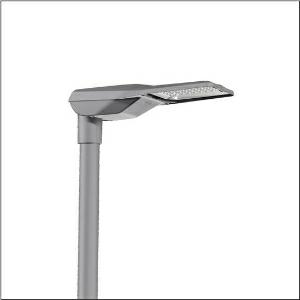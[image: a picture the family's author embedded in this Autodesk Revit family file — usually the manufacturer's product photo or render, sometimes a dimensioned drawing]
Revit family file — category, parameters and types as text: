
# Revit family: streetlight_sl_21_iq_mini___pl52_5xe2h31g08gb_d0f1
name_source: partatom
category: Lighting Fixtures
units: mm (PartAtom-declared; Revit-internal decimal feet)

## family parameters
Cut with Voids When Loaded = No
Host = Face
Light Source = No
Part Type = Normal
Room Calculation Point = No
Round Connector Dimension = Use Diameter
Shared = No

## types (1)
- --- (1 x LED, 5580 lm, 37.1 W, 3000K)
    Apparent Load = 37 VA
    CIE Flux Codes = 27 59 98 100 100
    Color Rendering = 70
    Color Temperature = 3000K
    Default Elevation = 1800 mm
    Description = Streetlight SL 21 iQ mini, mast luminaire, primary light control with lens, of PMMA, primary optical cover: cover, of toughened safety glass, transparent, light distribution: PL52, light emission: direct distribution, primary light characteristic: asymmetric, installation type: post-top, side-entry, LED, High Power LED, rated luminous flux: 5.580lm, luminous efficacy: 150lm/W, light colour: 730, colour temperature: 3000K, control gear: iQ Street-Remote, control: Street-Remote, Auto-Match, Temp-Guard, Lumen-Switch, Night-Set, Smart-Wire, Light-Fading, Desk-Remote (wireless, voltage-free reading and setting of iQ features in the workshop via application-optimized NFC function/RFID function), optimised constant luminous flux control (CLO 2.0), pre-setting: linear dimming characteristic, mains connection: 220..240V, AC, 50/60Hz, start of lifetime: 37W, end of service life: 39W, reduction: 18W, luminaire housing, of diecast aluminium, powder-coated, SITECO metallic grey (DB 702S), corrosivity category C5 high according to DIN EN ISO 12944, please order mast flange separately, inclination adjustable: 0°, 5°, 10°, 15°, sealing non-destructively replaceable, multi-level sealing system, length: 628mm, width: 235mm, height: 110mm, mast flange for spigot size: 42mm (side-entry): 5XC10008XM4, 60/48mm (side-entry/post-top): 5XC10108XM2, 76/60mm (side-entry/post-top): 5XC10108XM1, mounting height: 4..8m, protection rating (complete): IP66, insulation class (complete): insulation class II (safety insulation), certification: CE, ENEC, ENEC+, VDE, impact resistance: IK10, permissible operating ambient temperature for outdoor applications: -40..+50°C, standard-compliant lighting for roads and squares, packaging unit: 1 piece

Light Distribution: PL52
    Height = 110 mm
    Lamp = 1 x LED
    Lamp Light Flux = 5580 lm
    Lamp Power = 37.1 W
    Lamp count = 1
    Length = 625 mm
    Luminous efficacy = 150 lm/W
    Manufacturer = Siteco
    ModVariant = No
    Model = 5XE2H31G08GB
    Number of Poles = 1
    OnlyDefault = Yes
    Power Factor = 1
    Product Name = Streetlight SL 21 iQ mini | PL52
    Product group = mast luminaire | pylon top
    ProductGroupID = 6100
    Protection Class = Protection class II
    Protection Degree = IP 66
    RLX_Detail_Level = 1
    RLX_Emergency_Light_Flux = 0 lm
    RLX_Emergency_Type = 0
    RLX_Emergency_Type_DB = No
    RlxData = <blob elided: 35909 chars, md5=795601a6>
    Socket = socket
    Standby Power = 0 W
    System Light Flux = 5580 lm
    System Power = 37 W
    Type Comments = factory setting: luminous flux: 100 % | dim-lin: 254 | 385 mA
    Type Image = l_1003519.jpg
    URL = http://relux.com
    VarID = @adj_187783
    Voltage = 0 V
    Weight = 0.00 kg
    Width = 234 mm

## geometry (parser evidence)
native form markers: Blend x4, Sweep x10
no freeform markers — native parametric forms only
